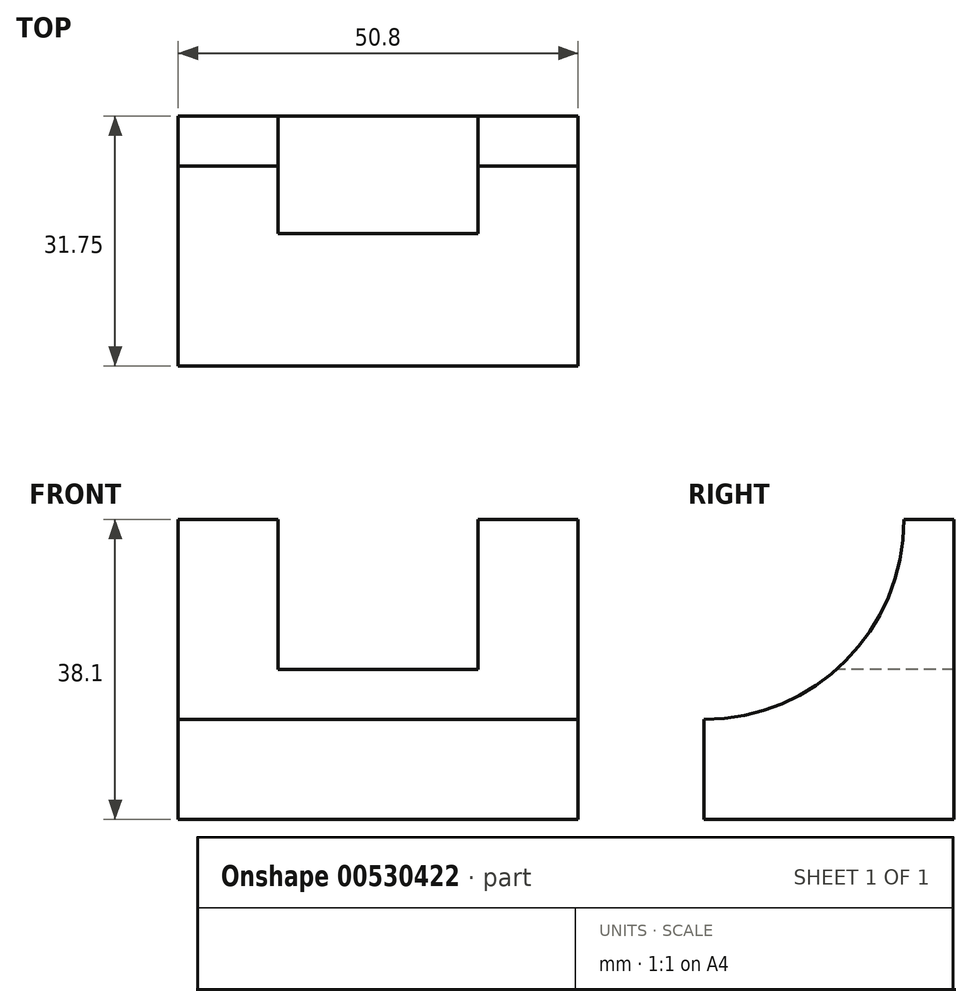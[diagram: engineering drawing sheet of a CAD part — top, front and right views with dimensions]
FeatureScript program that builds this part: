
annotation { "Feature Type Name" : "Feature", "Feature Type Description" : "" }
export const myFeature = defineFeature(function(context is Context, id is Id, definition is map)
    precondition{}
    {
        {
            var Q0;
            Q0=qCreatedBy(makeId("Front.planeOp"),FACE);
            var sketch = newSketch(context, id + "F0", { "sketchPlane" : qUnion([Q0])});
            skLineSegment(sketch, "E0", {"start": v(0, 38.1) * mm, "end": v(0, 0) * mm});
            skLineSegment(sketch, "E1", {"start": v(0, 0) * mm, "end": v(50.8, 0) * mm});
            skLineSegment(sketch, "E2", {"start": v(0, 38.1) * mm, "end": v(50.8, 38.1) * mm});
            skLineSegment(sketch, "E3", {"start": v(50.8, 38.1) * mm, "end": v(50.8, 0) * mm});
            skSolve(sketch);
        }
        {
            var Q0;
            Q0=makeQuery(id+"F0.imprint","IMPRINT",FACE,{"disambiguationData":[TD([[makeQuery(id+"F0.imprint","IMPRINT",EDGE,{"derivedFrom":sQuery(id+"F0.wireOp",EDGE,"E0")}),1.0]])]});
            extrude(context, id + "F1", {"entities" : qUnion([Q0]), "depth" : 31.75 * mm, "offsetDistance" : 25.4 * mm});
        }
        {
            var Q0;
            Q0=makeQuery(id+"F1.opExtrude","CAP_FACE",FACE,{"disambiguationData":[OSD([sQuery(id+"F0.wireOp",EDGE,"E0"),sQuery(id+"F0.wireOp",EDGE,"E1"),sQuery(id+"F0.wireOp",EDGE,"E2"),sQuery(id+"F0.wireOp",EDGE,"E3")])],"isStart":false});
            var sketch = newSketch(context, id + "F2", { "sketchPlane" : qUnion([Q0])});
            skLineSegment(sketch, "E4", {"start": v(12.7, 38.1) * mm, "end": v(12.7, 19.05) * mm});
            skLineSegment(sketch, "E5", {"start": v(12.7, 19.05) * mm, "end": v(38.1, 19.05) * mm});
            skLineSegment(sketch, "E6", {"start": v(38.1, 19.05) * mm, "end": v(38.1, 38.1) * mm});
            skSolve(sketch);
        }
        {
            var Q0;
            {var subQ0=sQuery(id+"F2.wireOp",EDGE,"E4");Q0=makeQuery(id+"F2.imprint","IMPRINT",FACE,{"disambiguationData":[TD([[makeQuery(id+"F2.imprint","IMPRINT",EDGE,{"derivedFrom":subQ0}),1.0]])]});}
            extrude(context, id + "F3", {"entities" : qUnion([Q0]), "operationType" : NewBodyOperationType.REMOVE, "endBound" : BoundingType.THROUGH_ALL, "oppositeDirection" : true, "depth" : 25.4 * mm, "offsetDistance" : 25.4 * mm});
        }
        {
            var Q0;
            Q0=makeQuery(id+"F1.opExtrude","SWEPT_FACE",FACE,{"disambiguationData":[OSD([sQuery(id+"F0.wireOp",EDGE,"E3")])]});
            var sketch = newSketch(context, id + "F4", { "sketchPlane" : qUnion([Q0])});
            skCircle(sketch, "E7", {"center": v(-31.75, 38.1) * mm, "radius": 25.4 * mm});
            skSolve(sketch);
        }
        {
            var Q0;
            {var subQ0=sQuery(id+"F4.wireOp",EDGE,"E7");var subQ1=sQuery(id+"F0.wireOp",EDGE,"E3");var subQ4=makeQuery(id+"F1.opExtrude","CAP_EDGE",EDGE,{"disambiguationData":[OSD([subQ1])],"isStart":false});var subQ5=makeQuery(id+"F4.imprint","INTERSECT",VERTEX,{"derivedFrom":[subQ4,subQ0]});Q0=makeQuery(id+"F4.imprint","IMPRINT",FACE,{"disambiguationData":[TD([[makeQuery(id+"F4.imprint","IMPRINT",EDGE,{"disambiguationData":[TD([[subQ5,1.0]])],"derivedFrom":subQ0}),1.0]])]});}
            var Q1;
            {var subQ0=sQuery(id+"F4.wireOp",EDGE,"E7");var subQ1=sQuery(id+"F0.wireOp",EDGE,"E3");var subQ4=makeQuery(id+"F1.opExtrude","CAP_EDGE",EDGE,{"disambiguationData":[OSD([subQ1])],"isStart":false});var subQ5=makeQuery(id+"F4.imprint","INTERSECT",VERTEX,{"derivedFrom":[subQ4,subQ0]});Q1=makeQuery(id+"F4.imprint","IMPRINT",FACE,{"disambiguationData":[TD([[makeQuery(id+"F4.imprint","IMPRINT",EDGE,{"disambiguationData":[TD([[subQ5,-1.0]])],"derivedFrom":subQ0}),1.0]])]});}
            extrude(context, id + "F5", {"entities" : qUnion([Q0, Q1]), "operationType" : NewBodyOperationType.REMOVE, "oppositeDirection" : true, "depth" : 50.8 * mm, "offsetDistance" : 25.4 * mm});
        }
    });
